# Revit family: A-Series Casement2
name_source: partatom
category: Windows
revit_build: Autodesk Revit 2013 (Build: 20130531_2115(x64)
units: mm (PartAtom-declared; Revit-internal decimal feet)

## types (1)
- A-Series Casement2
    ..           Lights High = 3
    ..           Lights Wide = 3
    ..          Fractional Bar Location = 2' - 0"
    ..          Fractional Bar Size                                                                                                             Drop Down List = Bar Size : 3/4"
    ..          Lights High Above = 2
    ..          Lights High Below = 1
    ..          Lights Wide Above = 4
    ..          Lights Wide Below = 2
    ..    Specified Equal Light Pattern = No
    ..    Specified Fractional Pattern = No
    Analytic Construction = <None>
    Assembly Code = B2020100
    Between Glass Grille Bar = Yes
    Between Glass Grille Bar Finish = Stainless Steel - Andersen - Standard
    Default Sill Height = 3' - 0"
    Description = Composite-clad wood casement window
    Designation = Not a Type.  Load Type Catalog
    Exterior Grille Bar = Yes
    Exterior Trim                                                                                                             Drop Down List = Exterior Trim : No Exterior Trim
    Exterior Trim Finish = Fibrex Composite - Andersen - White
    Exterior Unit Finish = Fibrex Composite - Andersen - White
    Family Version = 1.1.16
    Fractional Grille Bar Size = 0' - 0 3/4"
    Frame Depth = 0' - 4 9/16"
    Glazing Material = Glass ‐ Andersen - Low-E4 SmartSun
    Grille Bar Pattern                                                                                                             Drop Down List = Pattern : Colonial
    Grille Bar Size = 0' - 0 3/4"
    Grille Bar Size                                                                                                             Drop Down List = Bar Size : 3/4"
    Height = 3' - 0"
    Interior Casing = Yes
    Interior Casing Size = 0' - 2 1/4"
    Interior Grille Bar = Yes
    Interior Material = Wood - Andersen - Pine
    Jamb = 1
    Jamb Condition                                                                                                             Drop Down List = Jamb : Extension Jamb
    Manufacturer = Andersen Corporation
    Masonry Opening Height = 0' - 0"
    Masonry Opening Width = 0' - 0"
    Model = A-Series Casement
    Pattern = 1
    Product Documentation Link = http://www.andersenwindows.com
    Product Type = 1
    Rough Height = 3' - 0 3/4"
    Rough Opening Offset = 0' - 0"
    Rough Width = 2' - 0 3/4"
    Standard Lights High = 3
    Standard Lights Wide = 3
    Trim = 0
    Type Comments = Fiberglass and Fibrex clad wood casement window
    URL = www.andersenwindows.com
    Wall Closure = By host
    Width = 2' - 0"
    [.75"] = Bar Size : 3/4"
    [.75"_GBG] = Bar Size : 3/4" GBG
    [.875"] = Bar Size : 7/8"
    [1"_GBG] = Bar Size : 1" GBG
    [1.125"] = Bar Size : 1 1/8"
    [2.25"] = Bar Size : 2 1/4"
    [3.5" Flat Casing] = Exterior Trim : 3 1/2" Flat Casing
    [4.5" Flat Casing] = Exterior Trim : 4 1/2" Flat Casing
    [Bar] = Bar Size : 3/4"
    [Brick Mould] = Exterior Trim : Brick Mould
    [Colonial] = Pattern : Colonial
    [DWR] = Jamb : Drywall Return
    [Fractional_Bar] = Bar Size : 3/4"
    [GBG] = No
    [Jamb] = Jamb : Extension Jamb
    [Modified_Colonial] = Pattern : Modified Colonial
    [No_Ext_Trim] = Exterior Trim : No Exterior Trim
    [No_Grilles] = No Grilles
    [No_Xjamb] = Jamb : No Extension Jamb
    [Pattern] = Pattern : Colonial
    [Prairie] = Pattern : Prairie
    [Prairie_Overall] = Pattern : Prairie
    [Short_Fractional] = Pattern : Short Fractional
    [Specified_Equal_Light] = Pattern : Specified Equal Light
    [Specified_Fractional_Light] = Pattern : Specified Fractional Light
    [Tall_Fractional] = Pattern : Tall Fractional
    [Trim] = Exterior Trim : No Exterior Trim
    [Xjamb] = Jamb : Extension Jamb

## geometry (parser evidence)
native form markers: Sweep x9
no freeform markers — native parametric forms only
